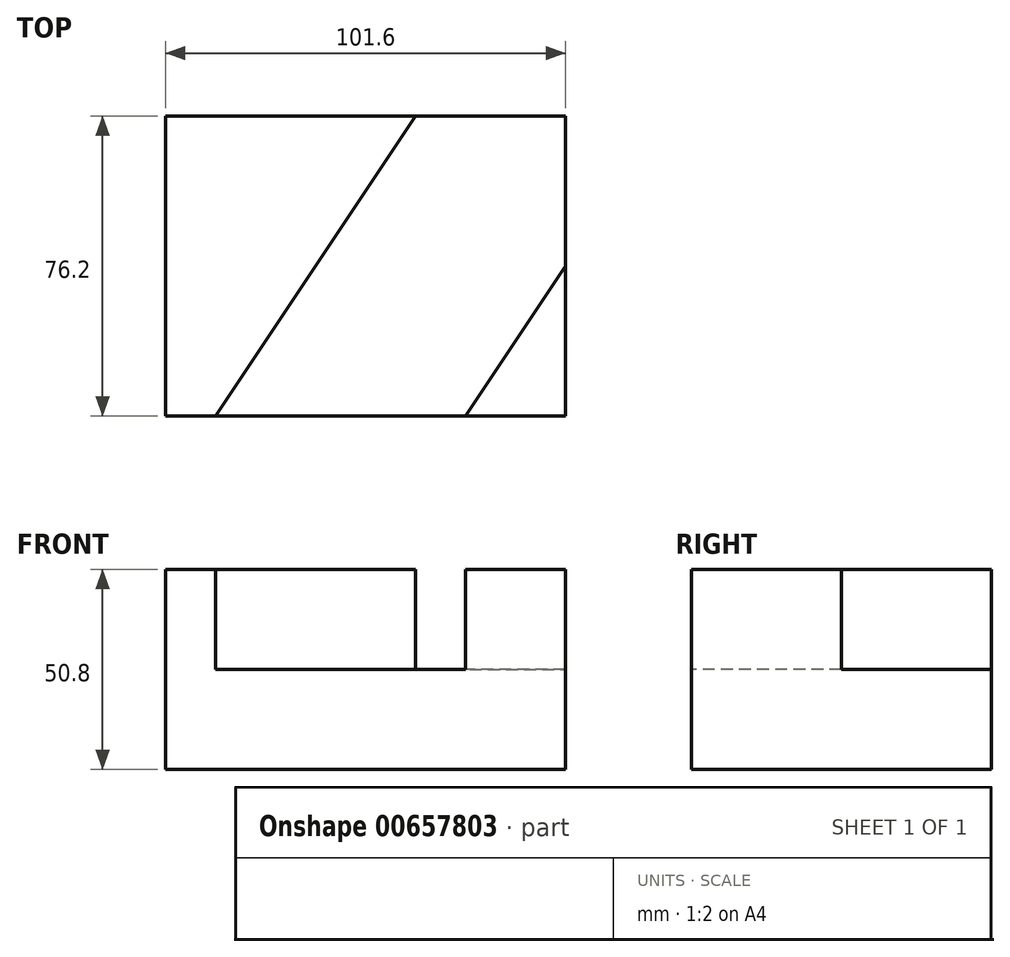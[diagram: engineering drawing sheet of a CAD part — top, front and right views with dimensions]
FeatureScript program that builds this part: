
annotation { "Feature Type Name" : "Feature", "Feature Type Description" : "" }
export const myFeature = defineFeature(function(context is Context, id is Id, definition is map)
    precondition{}
    {
        {
            var Q0;
            Q0=qCreatedBy(makeId("Front.planeOp"),FACE);
            var sketch = newSketch(context, id + "F0", { "sketchPlane" : qUnion([Q0])});
            skLineSegment(sketch, "E0.bottom", {"start": v(-56.7, -4.27) * mm, "end": v(44.9, -4.27) * mm});
            skLineSegment(sketch, "E0.top", {"start": v(-56.7, -29.67) * mm, "end": v(44.9, -29.67) * mm});
            skLineSegment(sketch, "E0.left", {"start": v(-56.7, -4.27) * mm, "end": v(-56.7, -29.67) * mm});
            skLineSegment(sketch, "E0.right", {"start": v(44.9, -4.27) * mm, "end": v(44.9, -29.67) * mm});
            skSolve(sketch);
        }
        {
            var Q0;
            Q0 = qSketchRegion(id + "F0", true);
            extrude(context, id + "F1", {"entities" : qUnion([Q0]), "depth" : 76.2 * mm, "offsetDistance" : 25.4 * mm});
        }
        {
            var Q0;
            Q0=makeQuery(id+"F1.opExtrude","SWEPT_FACE",FACE,{"disambiguationData":[OSD([sQuery(id+"F0.wireOp",EDGE,"E0.bottom")])]});
            var sketch = newSketch(context, id + "F2", { "sketchPlane" : qUnion([Q0])});
            skLineSegment(sketch, "E1", {"start": v(44.9, -76.2) * mm, "end": v(44.9, -38.1) * mm});
            skLineSegment(sketch, "E2", {"start": v(44.9, -38.1) * mm, "end": v(19.5, -76.2) * mm});
            skLineSegment(sketch, "E3", {"start": v(19.5, -76.2) * mm, "end": v(44.9, -76.2) * mm});
            skSolve(sketch);
        }
        {
            var Q0;
            Q0 = qSketchRegion(id + "F2", true);
            extrude(context, id + "F3", {"entities" : qUnion([Q0]), "operationType" : NewBodyOperationType.ADD, "depth" : 25.4 * mm, "offsetDistance" : 25.4 * mm});
        }
        {
            var Q0;
            Q0=makeQuery(id+"F1.opExtrude","SWEPT_FACE",FACE,{"disambiguationData":[OSD([sQuery(id+"F0.wireOp",EDGE,"E0.bottom")])]});
            var sketch = newSketch(context, id + "F4", { "sketchPlane" : qUnion([Q0])});
            skLineSegment(sketch, "E4", {"start": v(-56.7, -76.2) * mm, "end": v(-44, -76.2) * mm});
            skLineSegment(sketch, "E5", {"start": v(-56.7, 0) * mm, "end": v(6.8, 0) * mm});
            skLineSegment(sketch, "E6", {"start": v(6.8, 0) * mm, "end": v(-44, -76.2) * mm});
            skLineSegment(sketch, "E7", {"start": v(-56.7, 0) * mm, "end": v(-56.7, -76.2) * mm});
            skSolve(sketch);
        }
        {
            var Q0;
            Q0=makeQuery(id+"F4.imprint","IMPRINT",FACE,{"disambiguationData":[TD([[makeQuery(id+"F4.imprint","IMPRINT",EDGE,{"derivedFrom":sQuery(id+"F4.wireOp",EDGE,"E4")}),1.0]])]});
            extrude(context, id + "F5", {"entities" : qUnion([Q0]), "operationType" : NewBodyOperationType.ADD, "depth" : 25.4 * mm, "offsetDistance" : 25.4 * mm});
        }
    });
